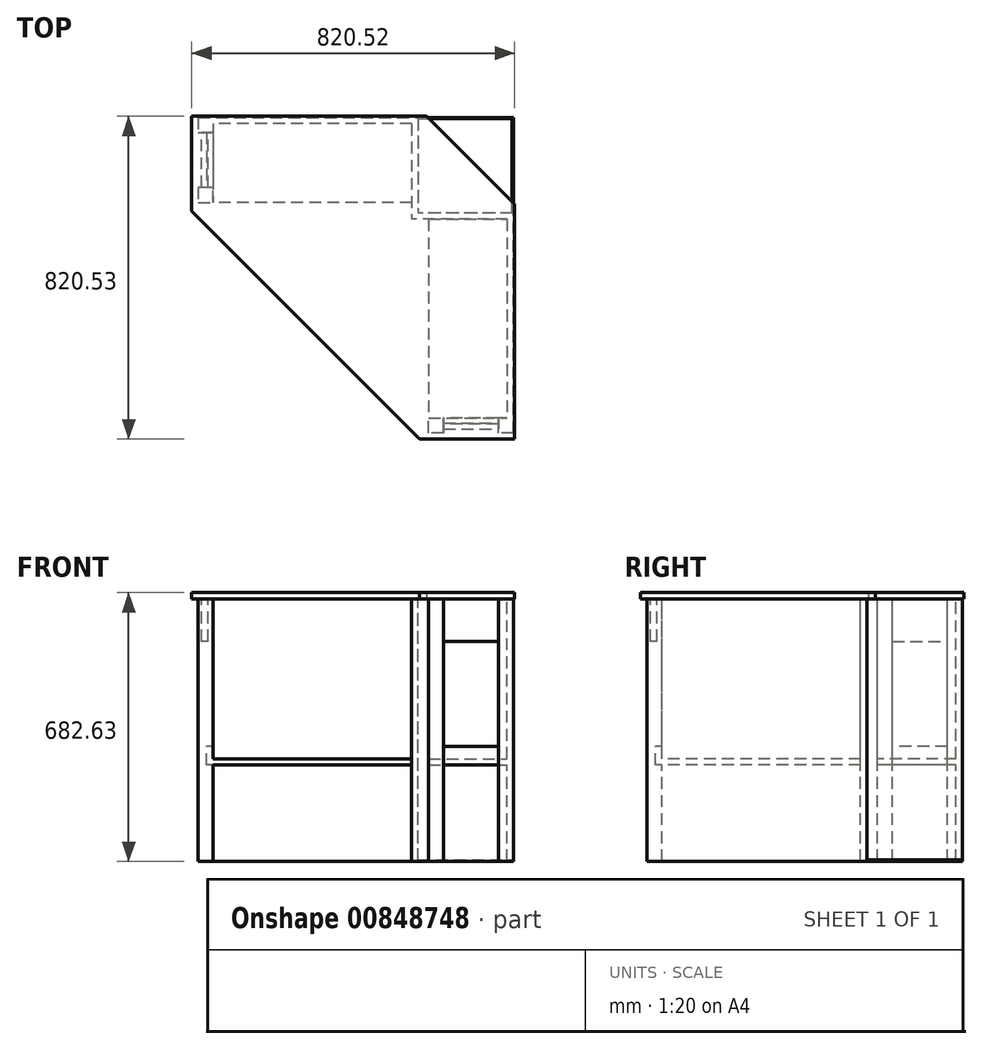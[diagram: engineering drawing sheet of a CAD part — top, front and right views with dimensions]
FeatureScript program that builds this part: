
annotation { "Feature Type Name" : "Feature", "Feature Type Description" : "" }
export const myFeature = defineFeature(function(context is Context, id is Id, definition is map)
    precondition{}
    {
        {
            var Q0;
            Q0=qCreatedBy(makeId("Top.planeOp"),FACE);
            var sketch = newSketch(context, id + "F0", { "sketchPlane" : qUnion([Q0])});
            skLineSegment(sketch, "E0", {"start": v(-419.83, 329.74) * mm, "end": v(177.07, 329.74) * mm});
            skLineSegment(sketch, "E1", {"start": v(-419.83, 329.74) * mm, "end": v(-419.83, 88.44) * mm});
            skLineSegment(sketch, "E2", {"start": v(-419.83, 88.44) * mm, "end": v(159.4, -490.79) * mm});
            skLineSegment(sketch, "E3", {"start": v(159.4, -490.79) * mm, "end": v(400.7, -490.79) * mm});
            skLineSegment(sketch, "E4", {"start": v(400.7, -490.79) * mm, "end": v(400.7, 106.11) * mm});
            skLineSegment(sketch, "E5", {"start": v(177.07, 329.74) * mm, "end": v(400.7, 106.11) * mm});
            skSolve(sketch);
        }
        {
            var Q0;
            Q0 = qSketchRegion(id + "F0", true);
            extrude(context, id + "F1", {"entities" : qUnion([Q0]), "depth" : 15.88 * mm, "offsetDistance" : 25.4 * mm});
        }
        {
            var Q0;
            Q0=makeQuery(id+"F1.opExtrude","CAP_FACE",FACE,{"disambiguationData":[OSD([sQuery(id+"F0.wireOp",EDGE,"E0"),sQuery(id+"F0.wireOp",EDGE,"E1"),sQuery(id+"F0.wireOp",EDGE,"E2"),sQuery(id+"F0.wireOp",EDGE,"E3"),sQuery(id+"F0.wireOp",EDGE,"E4"),sQuery(id+"F0.wireOp",EDGE,"E5")])],"isStart":true});
            var sketch = newSketch(context, id + "F2", { "sketchPlane" : qUnion([Q0])});
            skLineSegment(sketch, "E6", {"start": v(397.52, 474.91) * mm, "end": v(397.52, 436.81) * mm});
            skLineSegment(sketch, "E7", {"start": v(397.52, 474.91) * mm, "end": v(359.42, 474.91) * mm});
            skLineSegment(sketch, "E8", {"start": v(397.52, 436.81) * mm, "end": v(359.42, 436.81) * mm});
            skLineSegment(sketch, "E9", {"start": v(359.42, 474.91) * mm, "end": v(359.42, 465.39) * mm});
            skLineSegment(sketch, "E10", {"start": v(359.42, 465.39) * mm, "end": v(219.72, 465.39) * mm});
            skLineSegment(sketch, "E11", {"start": v(219.72, 465.39) * mm, "end": v(219.72, 474.91) * mm});
            skLineSegment(sketch, "E12", {"start": v(219.72, 474.91) * mm, "end": v(181.62, 474.91) * mm});
            skLineSegment(sketch, "E13", {"start": v(181.62, 474.91) * mm, "end": v(181.62, 436.81) * mm});
            skLineSegment(sketch, "E14", {"start": v(181.62, 436.81) * mm, "end": v(219.72, 436.81) * mm});
            skLineSegment(sketch, "E15", {"start": v(219.72, 465.39) * mm, "end": v(219.72, 449.51) * mm, "construction": true});
            skLineSegment(sketch, "E16", {"start": v(219.72, 449.51) * mm, "end": v(359.42, 449.51) * mm});
            skLineSegment(sketch, "E17.bottom", {"start": v(-403.96, -326.57) * mm, "end": v(-365.86, -326.57) * mm});
            skLineSegment(sketch, "E17.top", {"start": v(-403.96, -288.47) * mm, "end": v(-394.43, -288.47) * mm});
            skLineSegment(sketch, "E17.left", {"start": v(-403.96, -326.57) * mm, "end": v(-403.96, -288.47) * mm});
            skLineSegment(sketch, "E17.right", {"start": v(-365.86, -326.57) * mm, "end": v(-365.86, -288.47) * mm});
            skLineSegment(sketch, "E18", {"start": v(-394.43, -288.47) * mm, "end": v(-394.43, -148.77) * mm});
            skLineSegment(sketch, "E19", {"start": v(-378.56, -288.47) * mm, "end": v(-378.56, -148.77) * mm});
            skLineSegment(sketch, "E20", {"start": v(-378.56, -148.77) * mm, "end": v(-394.43, -148.77) * mm, "construction": true});
            skLineSegment(sketch, "E21", {"start": v(-394.43, -148.77) * mm, "end": v(-403.96, -148.77) * mm});
            skLineSegment(sketch, "E22", {"start": v(-403.96, -148.77) * mm, "end": v(-403.96, -110.67) * mm});
            skLineSegment(sketch, "E23", {"start": v(-403.96, -110.67) * mm, "end": v(-365.86, -110.67) * mm});
            skLineSegment(sketch, "E24", {"start": v(-365.86, -110.67) * mm, "end": v(-365.86, -148.77) * mm});
            skLineSegment(sketch, "E25", {"start": v(-365.86, -148.77) * mm, "end": v(-378.56, -148.77) * mm});
            skLineSegment(sketch, "E26", {"start": v(-378.56, -288.47) * mm, "end": v(-365.86, -288.47) * mm});
            skLineSegment(sketch, "E27", {"start": v(-394.43, -288.47) * mm, "end": v(-378.56, -288.47) * mm, "construction": true});
            skLineSegment(sketch, "E28", {"start": v(219.72, 449.51) * mm, "end": v(219.72, 436.81) * mm});
            skLineSegment(sketch, "E29", {"start": v(359.42, 465.39) * mm, "end": v(359.42, 449.51) * mm, "construction": true});
            skLineSegment(sketch, "E30", {"start": v(359.42, 449.51) * mm, "end": v(359.42, 436.81) * mm});
            skLineSegment(sketch, "E31", {"start": v(397.52, 436.81) * mm, "end": v(397.52, -83.89) * mm});
            skLineSegment(sketch, "E32", {"start": v(-365.86, -326.57) * mm, "end": v(154.84, -326.57) * mm});
            skLineSegment(sketch, "E33", {"start": v(-365.86, -310.7) * mm, "end": v(138.97, -310.7) * mm});
            skLineSegment(sketch, "E34", {"start": v(381.64, 436.81) * mm, "end": v(381.64, -68.01) * mm});
            skLineSegment(sketch, "E35", {"start": v(397.52, -83.89) * mm, "end": v(381.64, -83.89) * mm});
            skLineSegment(sketch, "E36", {"start": v(154.84, -326.57) * mm, "end": v(154.84, -310.7) * mm});
            skLineSegment(sketch, "E37", {"start": v(381.64, -68.01) * mm, "end": v(138.97, -68.01) * mm});
            skLineSegment(sketch, "E38", {"start": v(138.97, -310.7) * mm, "end": v(138.97, -68.01) * mm});
            skLineSegment(sketch, "E39", {"start": v(154.84, -310.7) * mm, "end": v(154.84, -83.89) * mm});
            skLineSegment(sketch, "E40", {"start": v(381.64, -83.89) * mm, "end": v(154.84, -83.89) * mm});
            skSolve(sketch);
        }
        {
            var Q0;
            Q0 = qSketchRegion(id + "F2", true);
            extrude(context, id + "F3", {"entities" : qUnion([Q0]), "operationType" : NewBodyOperationType.ADD, "depth" : 666.75 * mm, "offsetDistance" : 25.4 * mm});
        }
        {
            var Q0;
            Q0=makeQuery(id+"F3.opExtrude","SWEPT_FACE",FACE,{"disambiguationData":[OSD([sQuery(id+"F2.wireOp",EDGE,"E18")])]});
            var sketch = newSketch(context, id + "F4", { "sketchPlane" : qUnion([Q0])});
            skLineSegment(sketch, "E41", {"start": v(-148.77, -107.95) * mm, "end": v(-288.47, -107.95) * mm});
            skLineSegment(sketch, "E42", {"start": v(-288.47, -107.95) * mm, "end": v(-288.47, -374.65) * mm});
            skLineSegment(sketch, "E43", {"start": v(-288.47, -374.65) * mm, "end": v(-148.77, -374.65) * mm});
            skLineSegment(sketch, "E44", {"start": v(-148.77, -374.65) * mm, "end": v(-148.77, -107.95) * mm});
            skLineSegment(sketch, "E45", {"start": v(-288.47, -422.28) * mm, "end": v(-148.77, -422.28) * mm});
            skLineSegment(sketch, "E46", {"start": v(-148.77, -422.28) * mm, "end": v(-148.77, -666.75) * mm});
            skLineSegment(sketch, "E47", {"start": v(-148.77, -666.75) * mm, "end": v(-288.47, -666.75) * mm});
            skLineSegment(sketch, "E48", {"start": v(-288.47, -666.75) * mm, "end": v(-288.47, -422.28) * mm});
            skSolve(sketch);
        }
        {
            var Q0;
            Q0 = qSketchRegion(id + "F4", true);
            extrude(context, id + "F5", {"entities" : qUnion([Q0]), "operationType" : NewBodyOperationType.REMOVE, "oppositeDirection" : true, "depth" : 25.4 * mm, "offsetDistance" : 25.4 * mm});
        }
        {
            var Q0;
            Q0=makeQuery(id+"F5.boolean.opBoolean","SPLIT",FACE,{"disambiguationData":[TD([makeQuery(id+"F5.opExtrude","SWEPT_FACE",FACE,{"disambiguationData":[OSD([sQuery(id+"F4.wireOp",EDGE,"E43")])]})])],"derivedFrom":makeQuery(id+"F3.opExtrude","SWEPT_FACE",FACE,{"disambiguationData":[OSD([sQuery(id+"F2.wireOp",EDGE,"E19")])]})});
            var sketch = newSketch(context, id + "F6", { "sketchPlane" : qUnion([Q0])});
            skLineSegment(sketch, "E49.0", {"start": v(148.77, -422.28) * mm, "end": v(288.47, -422.28) * mm});
            skLineSegment(sketch, "E49.1", {"start": v(148.77, -374.65) * mm, "end": v(148.77, -422.28) * mm});
            skLineSegment(sketch, "E49.2", {"start": v(288.47, -374.65) * mm, "end": v(148.77, -374.65) * mm});
            skLineSegment(sketch, "E49.3", {"start": v(288.47, -422.28) * mm, "end": v(288.47, -374.65) * mm});
            skSolve(sketch);
        }
        {
            var Q0;
            Q0 = qSketchRegion(id + "F6", true);
            extrude(context, id + "F7", {"entities" : qUnion([Q0]), "operationType" : NewBodyOperationType.ADD, "depth" : 12.7 * mm, "offsetDistance" : 25.4 * mm});
        }
        {
            var Q0;
            Q0=makeQuery(id+"F5.boolean.opBoolean","SPLIT",FACE,{"disambiguationData":[TD([makeQuery(id+"F5.opExtrude","SWEPT_FACE",FACE,{"disambiguationData":[OSD([sQuery(id+"F4.wireOp",EDGE,"E43")])]})])],"derivedFrom":makeQuery(id+"F3.opExtrude","SWEPT_FACE",FACE,{"disambiguationData":[OSD([sQuery(id+"F2.wireOp",EDGE,"E18")])]})});
            var sketch = newSketch(context, id + "F8", { "sketchPlane" : qUnion([Q0])});
            skLineSegment(sketch, "E50.0", {"start": v(-288.47, -374.65) * mm, "end": v(-288.47, -422.28) * mm});
            skLineSegment(sketch, "E50.1", {"start": v(-148.77, -374.65) * mm, "end": v(-288.47, -374.65) * mm});
            skLineSegment(sketch, "E50.2", {"start": v(-148.77, -422.28) * mm, "end": v(-148.77, -374.65) * mm});
            skLineSegment(sketch, "E50.3", {"start": v(-288.47, -422.28) * mm, "end": v(-148.77, -422.28) * mm});
            skSolve(sketch);
        }
        {
            var Q0;
            Q0 = qSketchRegion(id + "F8", true);
            extrude(context, id + "F9", {"entities" : qUnion([Q0]), "operationType" : NewBodyOperationType.REMOVE, "oppositeDirection" : true, "depth" : 12.7 * mm, "offsetDistance" : 25.4 * mm});
        }
        {
            var Q0;
            Q0=makeQuery(id+"F3.opExtrude","SWEPT_FACE",FACE,{"disambiguationData":[OSD([sQuery(id+"F2.wireOp",EDGE,"E10")])]});
            var sketch = newSketch(context, id + "F10", { "sketchPlane" : qUnion([Q0])});
            skLineSegment(sketch, "E51", {"start": v(219.72, -107.95) * mm, "end": v(359.42, -107.95) * mm});
            skLineSegment(sketch, "E52", {"start": v(359.42, -107.95) * mm, "end": v(359.42, -374.65) * mm});
            skLineSegment(sketch, "E53", {"start": v(359.42, -374.65) * mm, "end": v(219.72, -374.65) * mm});
            skLineSegment(sketch, "E54", {"start": v(219.72, -374.65) * mm, "end": v(219.72, -107.95) * mm});
            skLineSegment(sketch, "E55", {"start": v(359.42, -422.28) * mm, "end": v(219.72, -422.28) * mm});
            skLineSegment(sketch, "E56", {"start": v(359.42, -422.28) * mm, "end": v(359.42, -666.75) * mm});
            skLineSegment(sketch, "E57", {"start": v(359.42, -666.75) * mm, "end": v(219.72, -666.75) * mm});
            skLineSegment(sketch, "E58", {"start": v(219.72, -666.75) * mm, "end": v(219.72, -422.28) * mm});
            skSolve(sketch);
        }
        {
            var Q0;
            Q0 = qSketchRegion(id + "F10", true);
            extrude(context, id + "F11", {"entities" : qUnion([Q0]), "operationType" : NewBodyOperationType.REMOVE, "oppositeDirection" : true, "depth" : 25.4 * mm, "offsetDistance" : 25.4 * mm});
        }
        {
            var Q0;
            Q0=makeQuery(id+"F11.boolean.opBoolean","SPLIT",FACE,{"disambiguationData":[TD([makeQuery(id+"F11.opExtrude","SWEPT_FACE",FACE,{"disambiguationData":[OSD([sQuery(id+"F10.wireOp",EDGE,"E53")])]})])],"derivedFrom":makeQuery(id+"F3.opExtrude","SWEPT_FACE",FACE,{"disambiguationData":[OSD([sQuery(id+"F2.wireOp",EDGE,"E16")])]})});
            var sketch = newSketch(context, id + "F12", { "sketchPlane" : qUnion([Q0])});
            skLineSegment(sketch, "E59.0", {"start": v(-359.42, -374.65) * mm, "end": v(-359.42, -422.28) * mm});
            skLineSegment(sketch, "E59.1", {"start": v(-219.72, -374.65) * mm, "end": v(-359.42, -374.65) * mm});
            skLineSegment(sketch, "E59.2", {"start": v(-219.72, -422.28) * mm, "end": v(-219.72, -374.65) * mm});
            skLineSegment(sketch, "E59.3", {"start": v(-359.42, -422.28) * mm, "end": v(-219.72, -422.28) * mm});
            skSolve(sketch);
        }
        {
            var Q0;
            Q0 = qSketchRegion(id + "F12", true);
            extrude(context, id + "F13", {"entities" : qUnion([Q0]), "operationType" : NewBodyOperationType.ADD, "depth" : 12.7 * mm, "offsetDistance" : 25.4 * mm});
        }
        {
            var Q0;
            Q0=makeQuery(id+"F11.boolean.opBoolean","SPLIT",FACE,{"disambiguationData":[TD([makeQuery(id+"F11.opExtrude","SWEPT_FACE",FACE,{"disambiguationData":[OSD([sQuery(id+"F10.wireOp",EDGE,"E53")])]})])],"derivedFrom":makeQuery(id+"F3.opExtrude","SWEPT_FACE",FACE,{"disambiguationData":[OSD([sQuery(id+"F2.wireOp",EDGE,"E10")])]})});
            var sketch = newSketch(context, id + "F14", { "sketchPlane" : qUnion([Q0])});
            skLineSegment(sketch, "E60.0", {"start": v(219.72, -422.28) * mm, "end": v(359.42, -422.28) * mm});
            skLineSegment(sketch, "E60.1", {"start": v(219.72, -374.65) * mm, "end": v(219.72, -422.28) * mm});
            skLineSegment(sketch, "E60.2", {"start": v(359.42, -374.65) * mm, "end": v(219.72, -374.65) * mm});
            skLineSegment(sketch, "E60.3", {"start": v(359.42, -422.28) * mm, "end": v(359.42, -374.65) * mm});
            skSolve(sketch);
        }
        {
            var Q0;
            Q0 = qSketchRegion(id + "F14", true);
            extrude(context, id + "F15", {"entities" : qUnion([Q0]), "operationType" : NewBodyOperationType.REMOVE, "oppositeDirection" : true, "depth" : 12.7 * mm, "offsetDistance" : 25.4 * mm});
        }
        {
            var Q0;
            Q0=makeQuery(id+"F7.boolean.opBoolean","MERGE",FACE,{"derivedFrom":[makeQuery(id+"F3.opExtrude","SWEPT_FACE",FACE,{"disambiguationData":[OSD([sQuery(id+"F2.wireOp",EDGE,"E17.right")])]}),makeQuery(id+"F3.opExtrude","SWEPT_FACE",FACE,{"disambiguationData":[OSD([sQuery(id+"F2.wireOp",EDGE,"E24")])]}),makeQuery(id+"F7.opExtrude","CAP_FACE",FACE,{"disambiguationData":[OSD([sQuery(id+"F6.wireOp",EDGE,"E49.0"),sQuery(id+"F6.wireOp",EDGE,"E49.1"),sQuery(id+"F6.wireOp",EDGE,"E49.2"),sQuery(id+"F6.wireOp",EDGE,"E49.3")])],"isStart":false})]});
            var sketch = newSketch(context, id + "F16", { "sketchPlane" : qUnion([Q0])});
            skLineSegment(sketch, "E61", {"start": v(288.47, -422.28) * mm, "end": v(310.7, -422.28) * mm});
            skLineSegment(sketch, "E62", {"start": v(310.7, -422.28) * mm, "end": v(310.7, -406.4) * mm});
            skLineSegment(sketch, "E63", {"start": v(310.7, -406.4) * mm, "end": v(110.67, -406.4) * mm});
            skLineSegment(sketch, "E64", {"start": v(288.47, -422.28) * mm, "end": v(148.77, -422.28) * mm});
            skLineSegment(sketch, "E65", {"start": v(148.77, -422.28) * mm, "end": v(110.67, -422.28) * mm});
            skLineSegment(sketch, "E66", {"start": v(110.67, -422.28) * mm, "end": v(110.67, -406.4) * mm});
            skSolve(sketch);
        }
        {
            var Q0;
            Q0 = qSketchRegion(id + "F16", true);
            extrude(context, id + "F17", {"entities" : qUnion([Q0]), "operationType" : NewBodyOperationType.ADD, "depth" : 504.82 * mm, "offsetDistance" : 25.4 * mm});
        }
        {
            var Q0;
            Q0=makeQuery(id+"F13.boolean.opBoolean","MERGE",FACE,{"derivedFrom":[makeQuery(id+"F3.opExtrude","SWEPT_FACE",FACE,{"disambiguationData":[OSD([sQuery(id+"F2.wireOp",EDGE,"E8")])]}),makeQuery(id+"F3.opExtrude","SWEPT_FACE",FACE,{"disambiguationData":[OSD([sQuery(id+"F2.wireOp",EDGE,"E14")])]}),makeQuery(id+"F13.opExtrude","CAP_FACE",FACE,{"disambiguationData":[OSD([sQuery(id+"F12.wireOp",EDGE,"E59.0"),sQuery(id+"F12.wireOp",EDGE,"E59.1"),sQuery(id+"F12.wireOp",EDGE,"E59.2"),sQuery(id+"F12.wireOp",EDGE,"E59.3")])],"isStart":false})]});
            var sketch = newSketch(context, id + "F18", { "sketchPlane" : qUnion([Q0])});
            skLineSegment(sketch, "E67", {"start": v(-359.42, -422.28) * mm, "end": v(-381.64, -422.28) * mm});
            skLineSegment(sketch, "E68", {"start": v(-359.42, -422.28) * mm, "end": v(-219.72, -422.28) * mm});
            skLineSegment(sketch, "E69", {"start": v(-219.72, -422.28) * mm, "end": v(-181.62, -422.28) * mm});
            skLineSegment(sketch, "E70", {"start": v(-181.62, -422.28) * mm, "end": v(-181.62, -406.4) * mm});
            skLineSegment(sketch, "E71", {"start": v(-181.62, -406.4) * mm, "end": v(-381.64, -406.4) * mm});
            skLineSegment(sketch, "E72", {"start": v(-381.64, -406.4) * mm, "end": v(-381.64, -422.28) * mm});
            skSolve(sketch);
        }
        {
            var Q0;
            Q0 = qSketchRegion(id + "F18", true);
            extrude(context, id + "F19", {"entities" : qUnion([Q0]), "operationType" : NewBodyOperationType.ADD, "depth" : 504.82 * mm, "offsetDistance" : 25.4 * mm});
        }
        {
            var Q0;
            {var subQ0=sQuery(id+"F2.wireOp",EDGE,"E34");var subQ4=sQuery(id+"F2.wireOp",EDGE,"E38");var subQ6=sQuery(id+"F2.wireOp",EDGE,"E37");var subQ8=sQuery(id+"F2.wireOp",EDGE,"E39");var subQ9=sQuery(id+"F2.wireOp",EDGE,"E36");var subQ11=sQuery(id+"F2.wireOp",EDGE,"E17.left");var subQ13=sQuery(id+"F2.wireOp",EDGE,"E40");var subQ14=sQuery(id+"F2.wireOp",EDGE,"E35");var subQ16=sQuery(id+"F2.wireOp",EDGE,"E9");var subQ18=sQuery(id+"F2.wireOp",EDGE,"E8");var subQ20=sQuery(id+"F2.wireOp",EDGE,"E17.right");var subQ22=sQuery(id+"F2.wireOp",EDGE,"E33");var subQ24=sQuery(id+"F2.wireOp",EDGE,"E7");var subQ25=makeQuery(id+"F3.opExtrude","SWEPT_FACE",FACE,{"disambiguationData":[OSD([subQ24])]});var subQ26=sQuery(id+"F2.wireOp",EDGE,"E30");var subQ28=sQuery(id+"F2.wireOp",EDGE,"E31");var subQ29=sQuery(id+"F2.wireOp",EDGE,"E6");var subQ31=sQuery(id+"F2.wireOp",EDGE,"E17.top");var subQ33=sQuery(id+"F2.wireOp",EDGE,"E32");var subQ34=sQuery(id+"F2.wireOp",EDGE,"E17.bottom");var subQ36=sQuery(id+"F2.wireOp",EDGE,"E26");var subQ38=sQuery(id+"F2.wireOp",EDGE,"E24");var subQ39=sQuery(id+"F2.wireOp",EDGE,"E28");var subQ40=sQuery(id+"F2.wireOp",EDGE,"E10");var subQ41=sQuery(id+"F2.wireOp",EDGE,"E11");var subQ42=sQuery(id+"F2.wireOp",EDGE,"E12");var subQ43=sQuery(id+"F2.wireOp",EDGE,"E13");var subQ44=sQuery(id+"F2.wireOp",EDGE,"E14");var subQ45=sQuery(id+"F2.wireOp",EDGE,"E16");Q0=makeQuery(id+"F11.boolean.opBoolean","SPLIT",FACE,{"disambiguationData":[TD([subQ25])],"derivedFrom":makeQuery(id+"F5.boolean.opBoolean","SPLIT",FACE,{"disambiguationData":[TD([subQ25])],"derivedFrom":makeQuery(id+"F3.opExtrude","CAP_FACE",FACE,{"disambiguationData":[OSD([subQ29,subQ24,subQ18,subQ16,subQ40,subQ41,subQ42,subQ43,subQ44,subQ45,subQ34,subQ31,subQ11,subQ20,sQuery(id+"F2.wireOp",EDGE,"E18"),sQuery(id+"F2.wireOp",EDGE,"E19"),sQuery(id+"F2.wireOp",EDGE,"E21"),sQuery(id+"F2.wireOp",EDGE,"E22"),sQuery(id+"F2.wireOp",EDGE,"E23"),subQ38,sQuery(id+"F2.wireOp",EDGE,"E25"),subQ36,subQ39,subQ26,subQ28,subQ33,subQ22,subQ0,subQ14,subQ9,subQ6,subQ4,subQ8,subQ13])],"isStart":false})})});}
            var sketch = newSketch(context, id + "F20", { "sketchPlane" : qUnion([Q0])});
            skLineSegment(sketch, "E73", {"start": v(154.84, -326.57) * mm, "end": v(397.52, -326.57) * mm});
            skLineSegment(sketch, "E74", {"start": v(397.52, -83.89) * mm, "end": v(397.52, -326.57) * mm});
            skLineSegment(sketch, "E75", {"start": v(154.84, -323.4) * mm, "end": v(394.34, -323.4) * mm});
            skLineSegment(sketch, "E76", {"start": v(394.34, -83.89) * mm, "end": v(394.34, -323.4) * mm});
            skLineSegment(sketch, "E77", {"start": v(397.52, -83.89) * mm, "end": v(394.34, -83.89) * mm});
            skLineSegment(sketch, "E78", {"start": v(154.84, -326.57) * mm, "end": v(154.84, -323.4) * mm});
            skSolve(sketch);
        }
        {
            var Q0;
            Q0 = qSketchRegion(id + "F20", true);
            extrude(context, id + "F21", {"entities" : qUnion([Q0]), "operationType" : NewBodyOperationType.ADD, "oppositeDirection" : true, "depth" : 3.17 * mm, "offsetDistance" : 25.4 * mm});
        }
    });
